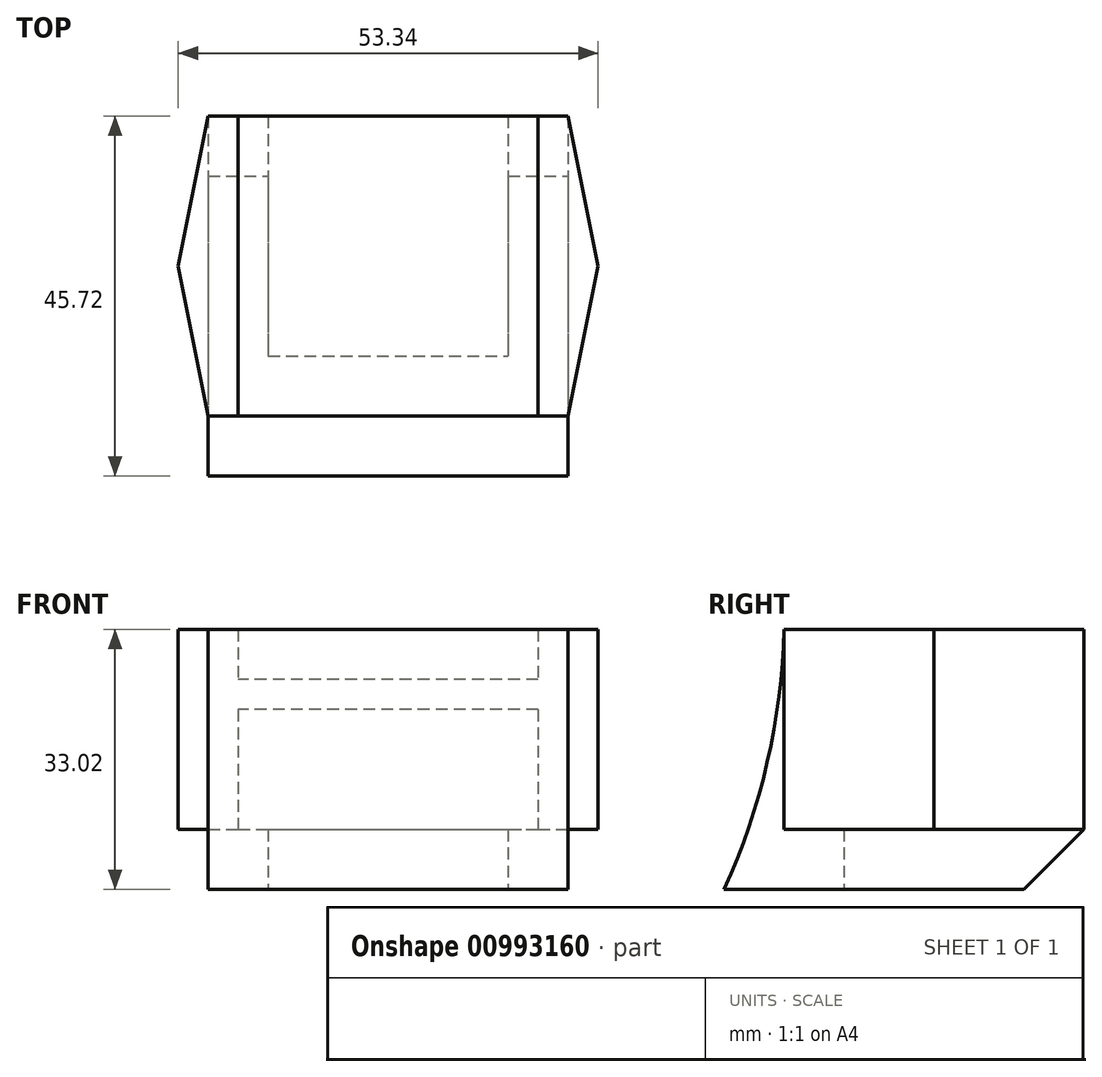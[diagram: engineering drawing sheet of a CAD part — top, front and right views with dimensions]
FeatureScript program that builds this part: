
annotation { "Feature Type Name" : "Feature", "Feature Type Description" : "" }
export const myFeature = defineFeature(function(context is Context, id is Id, definition is map)
    precondition{}
    {
        {
            var Q0;
            Q0=qCreatedBy(makeId("Top.planeOp"),FACE);
            var sketch = newSketch(context, id + "F0", { "sketchPlane" : qUnion([Q0])});
            skLineSegment(sketch, "E0.bottom", {"start": v(-55.91, -3.24) * mm, "end": v(-10.2, -3.24) * mm});
            skLineSegment(sketch, "E0.top", {"start": v(-55.91, -41.34) * mm, "end": v(-10.2, -41.34) * mm});
            skLineSegment(sketch, "E0.left", {"start": v(-55.91, -3.24) * mm, "end": v(-55.91, -41.34) * mm});
            skLineSegment(sketch, "E0.right", {"start": v(-10.2, -3.24) * mm, "end": v(-10.2, -41.34) * mm});
            skLineSegment(sketch, "E1.bottom", {"start": v(-48.3, -3.24) * mm, "end": v(-17.81, -3.24) * mm});
            skLineSegment(sketch, "E1.top", {"start": v(-48.3, -33.72) * mm, "end": v(-17.81, -33.72) * mm});
            skLineSegment(sketch, "E1.left", {"start": v(-48.3, -3.24) * mm, "end": v(-48.3, -33.72) * mm});
            skLineSegment(sketch, "E1.right", {"start": v(-17.81, -3.24) * mm, "end": v(-17.81, -33.72) * mm});
            skSolve(sketch);
        }
        {
            var Q0;
            Q0=makeQuery(id+"F0.imprint","IMPRINT",FACE,{"disambiguationData":[TD([[makeQuery(id+"F0.imprint","IMPRINT",EDGE,{"derivedFrom":sQuery(id+"F0.wireOp",EDGE,"E0.top")}),1.0]])]});
            extrude(context, id + "F1", {"entities" : qUnion([Q0]), "depth" : 7.62 * mm, "offsetDistance" : 25.4 * mm});
        }
        {
            var Q0;
            Q0=makeQuery(id+"F1.opExtrude","SWEPT_FACE",FACE,{"disambiguationData":[OSD([sQuery(id+"F0.wireOp",EDGE,"E0.right")])]});
            var sketch = newSketch(context, id + "F2", { "sketchPlane" : qUnion([Q0])});
            skLineSegment(sketch, "E2", {"start": v(-3.24, 7.62) * mm, "end": v(-10.86, 0) * mm});
            skSolve(sketch);
        }
        {
            var Q0;
            {var subQ0=sQuery(id+"F2.wireOp",EDGE,"E2");Q0=makeQuery(id+"F2.imprint","IMPRINT",FACE,{"disambiguationData":[TD([[makeQuery(id+"F2.imprint","IMPRINT",EDGE,{"derivedFrom":subQ0}),1.0]])]});}
            extrude(context, id + "F3", {"entities" : qUnion([Q0]), "operationType" : NewBodyOperationType.REMOVE, "oppositeDirection" : true, "depth" : 50.8 * mm, "offsetDistance" : 25.4 * mm});
        }
        {
            var Q0;
            Q0=makeQuery(id+"F1.opExtrude","SWEPT_FACE",FACE,{"disambiguationData":[OSD([sQuery(id+"F0.wireOp",EDGE,"E0.top")])]});
            var sketch = newSketch(context, id + "F4", { "sketchPlane" : qUnion([Q0])});
            skLineSegment(sketch, "E3.bottom", {"start": v(-55.91, 0) * mm, "end": v(-10.2, 0) * mm});
            skLineSegment(sketch, "E3.top", {"start": v(-55.91, 45.72) * mm, "end": v(-10.2, 45.72) * mm});
            skLineSegment(sketch, "E3.left", {"start": v(-55.91, 0) * mm, "end": v(-55.91, 45.72) * mm});
            skLineSegment(sketch, "E3.right", {"start": v(-10.2, 0) * mm, "end": v(-10.2, 45.72) * mm});
            skSolve(sketch);
        }
        {
            var Q0;
            {var subQ0=sQuery(id+"F4.wireOp",EDGE,"E3.top");Q0=makeQuery(id+"F4.imprint","IMPRINT",FACE,{"disambiguationData":[TD([[makeQuery(id+"F4.imprint","IMPRINT",EDGE,{"derivedFrom":subQ0}),-1.0]])]});}
            var Q1;
            {var subQ0=sQuery(id+"F4.wireOp",EDGE,"E3.bottom");Q1=makeQuery(id+"F4.imprint","IMPRINT",FACE,{"disambiguationData":[TD([[makeQuery(id+"F4.imprint","IMPRINT",EDGE,{"derivedFrom":subQ0}),1.0]])]});}
            extrude(context, id + "F5", {"entities" : qUnion([Q0, Q1]), "operationType" : NewBodyOperationType.ADD, "depth" : 7.62 * mm, "offsetDistance" : 25.4 * mm});
        }
        {
            var Q0;
            Q0=makeQuery(id+"F5.boolean.opBoolean","MERGE",FACE,{"derivedFrom":[makeQuery(id+"F1.opExtrude","SWEPT_FACE",FACE,{"disambiguationData":[OSD([sQuery(id+"F0.wireOp",EDGE,"E0.right")])]}),makeQuery(id+"F5.opExtrude","SWEPT_FACE",FACE,{"disambiguationData":[OSD([sQuery(id+"F4.wireOp",EDGE,"E3.right")])]})]});
            var sketch = newSketch(context, id + "F6", { "sketchPlane" : qUnion([Q0])});
            skArc(sketch, "E4", {"start": v(-48.96, 0) * mm, "mid": v(-43.48, 16.12) * mm, "end": v(-41.34, 33.02) * mm});
            skSolve(sketch);
        }
        {
            var Q0;
            {var subQ0=sQuery(id+"F6.wireOp",EDGE,"E4");Q0=makeQuery(id+"F6.imprint","IMPRINT",FACE,{"disambiguationData":[TD([[makeQuery(id+"F6.imprint","IMPRINT",EDGE,{"derivedFrom":subQ0}),1.0]])]});}
            extrude(context, id + "F7", {"entities" : qUnion([Q0]), "operationType" : NewBodyOperationType.REMOVE, "oppositeDirection" : true, "depth" : 50.8 * mm, "offsetDistance" : 25.4 * mm});
        }
        {
            var Q0;
            Q0=makeQuery(id+"F1.opExtrude","CAP_FACE",FACE,{"disambiguationData":[OSD([sQuery(id+"F0.wireOp",EDGE,"E0.bottom"),sQuery(id+"F0.wireOp",EDGE,"E0.top"),sQuery(id+"F0.wireOp",EDGE,"E0.left"),sQuery(id+"F0.wireOp",EDGE,"E0.right"),sQuery(id+"F0.wireOp",EDGE,"E1.top"),sQuery(id+"F0.wireOp",EDGE,"E1.left"),sQuery(id+"F0.wireOp",EDGE,"E1.right")])],"isStart":false});
            var sketch = newSketch(context, id + "F8", { "sketchPlane" : qUnion([Q0])});
            skLineSegment(sketch, "E5", {"start": v(-10.2, -41.34) * mm, "end": v(-6.38, -22.3) * mm});
            skPoint(sketch, "E5.endSnap0", {"position": v(-10.2, -22.3) * mm});
            skLineSegment(sketch, "E6", {"start": v(-6.38, -22.3) * mm, "end": v(-10.2, -3.24) * mm});
            skLineSegment(sketch, "E7", {"start": v(-59.72, -22.3) * mm, "end": v(-55.91, -41.34) * mm});
            skPoint(sketch, "E7.startSnap0", {"position": v(-55.91, -22.3) * mm});
            skLineSegment(sketch, "E8", {"start": v(-59.72, -22.3) * mm, "end": v(-55.91, -3.24) * mm});
            skLineSegment(sketch, "E9", {"start": v(-14, -3.24) * mm, "end": v(-14, -41.34) * mm});
            skLineSegment(sketch, "E10", {"start": v(-52.1, -3.24) * mm, "end": v(-52.1, -41.34) * mm});
            skSolve(sketch);
        }
        {
            var Q0;
            Q0=makeQuery(id+"F8.imprint","IMPRINT",FACE,{"disambiguationData":[TD([[makeQuery(id+"F8.imprint","IMPRINT",EDGE,{"derivedFrom":sQuery(id+"F8.wireOp",EDGE,"E5")}),1.0]])]});
            var Q1;
            {var subQ0=sQuery(id+"F8.wireOp",EDGE,"E9");Q1=makeQuery(id+"F8.imprint","IMPRINT",FACE,{"disambiguationData":[TD([[makeQuery(id+"F8.imprint","IMPRINT",EDGE,{"derivedFrom":subQ0}),1.0]])]});}
            var Q2;
            {var subQ0=sQuery(id+"F8.wireOp",EDGE,"E10");Q2=makeQuery(id+"F8.imprint","IMPRINT",FACE,{"disambiguationData":[TD([[makeQuery(id+"F8.imprint","IMPRINT",EDGE,{"derivedFrom":subQ0}),-1.0]])]});}
            var Q3;
            Q3=makeQuery(id+"F8.imprint","IMPRINT",FACE,{"disambiguationData":[TD([[makeQuery(id+"F8.imprint","IMPRINT",EDGE,{"derivedFrom":sQuery(id+"F8.wireOp",EDGE,"E7")}),1.0]])]});
            extrude(context, id + "F9", {"entities" : qUnion([Q0, Q1, Q2, Q3]), "operationType" : NewBodyOperationType.ADD, "depth" : 25.4 * mm, "offsetDistance" : 25.4 * mm});
        }
        {
            var Q0;
            Q0=makeQuery(id+"F9.opExtrude","SWEPT_FACE",FACE,{"disambiguationData":[OSD([sQuery(id+"F8.wireOp",EDGE,"E10")])]});
            var sketch = newSketch(context, id + "F10", { "sketchPlane" : qUnion([Q0])});
            skLineSegment(sketch, "E11.bottom", {"start": v(-41.34, 26.67) * mm, "end": v(-3.24, 26.67) * mm});
            skLineSegment(sketch, "E11.top", {"start": v(-41.34, 22.86) * mm, "end": v(-3.24, 22.86) * mm});
            skLineSegment(sketch, "E11.left", {"start": v(-41.34, 26.67) * mm, "end": v(-41.34, 22.86) * mm});
            skLineSegment(sketch, "E11.right", {"start": v(-3.24, 26.67) * mm, "end": v(-3.24, 22.86) * mm});
            skSolve(sketch);
        }
        {
            var Q0;
            Q0=makeQuery(id+"F10.imprint","IMPRINT",FACE,{"disambiguationData":[TD([[makeQuery(id+"F10.imprint","IMPRINT",EDGE,{"derivedFrom":sQuery(id+"F10.wireOp",EDGE,"E11.bottom")}),-1.0]])]});
            extrude(context, id + "F11", {"entities" : qUnion([Q0]), "operationType" : NewBodyOperationType.ADD, "depth" : 38.1 * mm, "offsetDistance" : 25.4 * mm});
        }
    });
